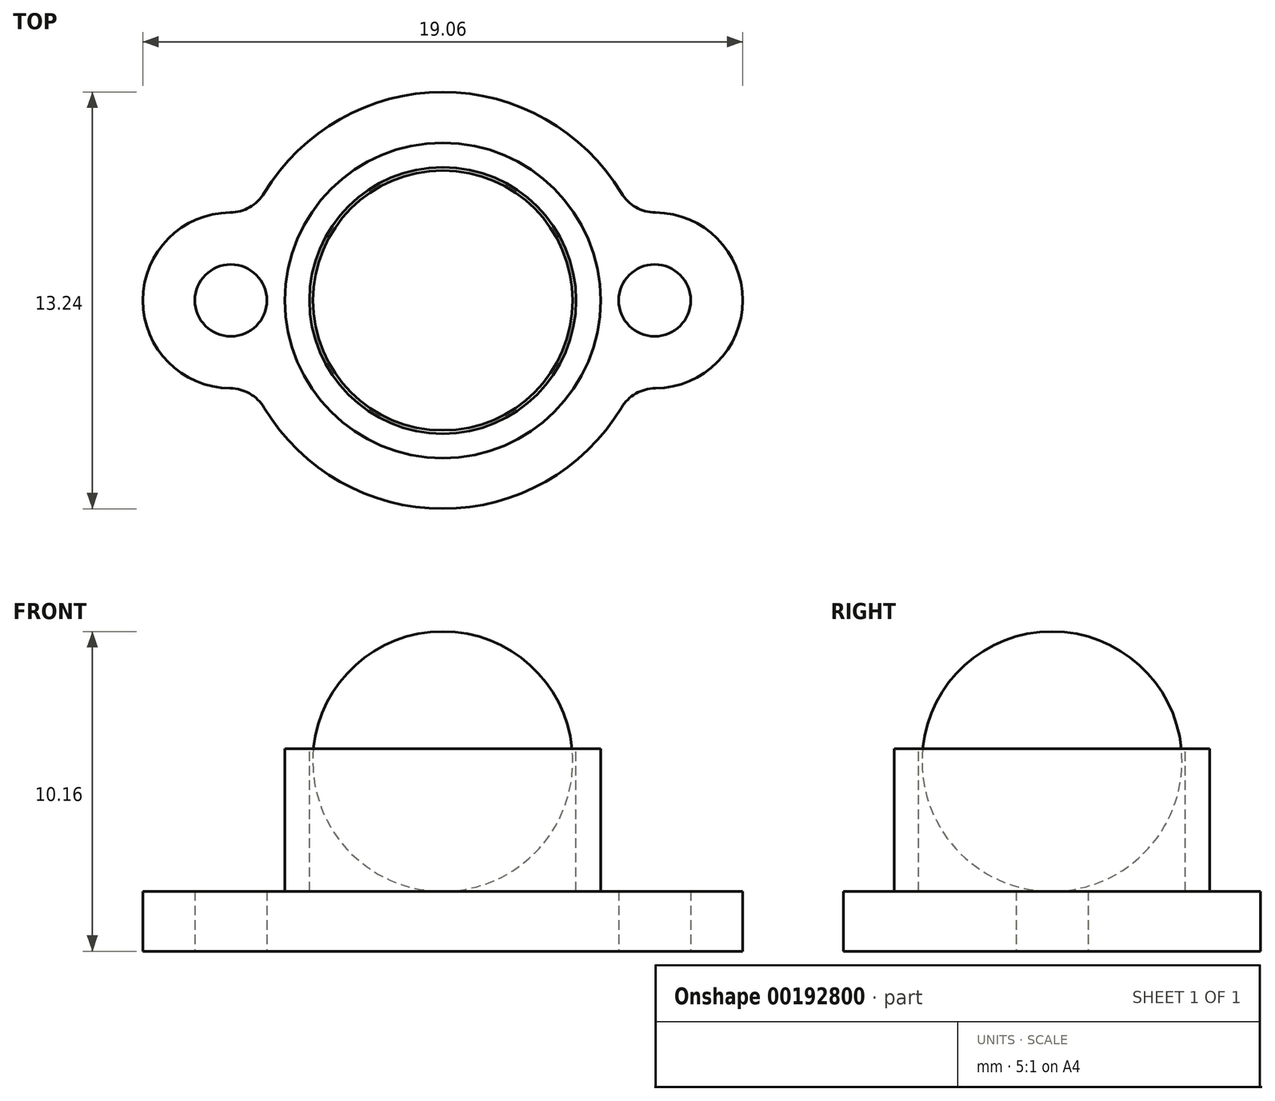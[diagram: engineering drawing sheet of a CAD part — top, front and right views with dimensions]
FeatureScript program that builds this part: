
annotation { "Feature Type Name" : "Feature", "Feature Type Description" : "" }
export const myFeature = defineFeature(function(context is Context, id is Id, definition is map)
    precondition{}
    {
        {
            var Q0;
            Q0=qCreatedBy(makeId("Top.planeOp"),FACE);
            var sketch = newSketch(context, id + "F0", { "sketchPlane" : qUnion([Q0])});
            skArc(sketch, "E0", {"start": v(-5.67, -3.4) * mm, "mid": v(0, -6.62) * mm, "end": v(5.67, -3.4) * mm});
            skCircle(sketch, "E1", {"center": v(-6.73, 0) * mm, "radius": 1.14 * mm});
            skArc(sketch, "E2", {"start": v(-6.75, 2.8) * mm, "mid": v(-9.53, 0) * mm, "end": v(-6.75, -2.8) * mm});
            skPoint(sketch, "E3.visualSharp", {"position": v(-6.04, 2.7) * mm});
            skArc(sketch, "E3.filletArc", {"start": v(-6.75, 2.8) * mm, "mid": v(-6.13, 2.96) * mm, "end": v(-5.67, 3.4) * mm});
            skPoint(sketch, "E4.visualSharp", {"position": v(-6.04, -2.7) * mm});
            skArc(sketch, "E4.filletArc", {"start": v(-5.67, -3.4) * mm, "mid": v(-6.13, -2.96) * mm, "end": v(-6.75, -2.8) * mm});
            skArc(sketch, "E5.MirrorCS", {"start": v(5.67, -3.4) * mm, "mid": v(6.13, -2.96) * mm, "end": v(6.75, -2.8) * mm});
            skArc(sketch, "E6.MirrorCS", {"start": v(6.75, 2.8) * mm, "mid": v(6.13, 2.96) * mm, "end": v(5.67, 3.4) * mm});
            skPoint(sketch, "E7.MirrorP", {"position": v(6.04, -2.7) * mm});
            skCircle(sketch, "E8.MirrorC", {"center": v(6.73, 0) * mm, "radius": 1.14 * mm});
            skArc(sketch, "E9.MirrorCS", {"start": v(6.75, 2.8) * mm, "mid": v(9.53, 0) * mm, "end": v(6.75, -2.8) * mm});
            skPoint(sketch, "E10.MirrorP", {"position": v(6.04, 2.7) * mm});
            skArc(sketch, "E11.trimOffspring", {"start": v(5.67, 3.4) * mm, "mid": v(0, 6.62) * mm, "end": v(-5.67, 3.4) * mm});
            skSolve(sketch);
        }
        {
            var Q0;
            Q0=qSketchRegion(id+"F0",true);
            extrude(context, id + "F1", {"entities" : qUnion([Q0]), "depth" : 1.9 * mm});
        }
        {
            var Q0;
            Q0=qCreatedBy(makeId("Front.planeOp"),FACE);
            var sketch = newSketch(context, id + "F2", { "sketchPlane" : qUnion([Q0])});
            skLineSegment(sketch, "E12", {"start": v(0, 10.16) * mm, "end": v(0, 1.9) * mm});
            skArc(sketch, "E13", {"start": v(0, 1.9) * mm, "mid": v(4.13, 6.03) * mm, "end": v(0, 10.16) * mm});
            skSolve(sketch);
        }
        {
            var Q0;
            Q0=qSketchRegion(id+"F2",true);
            var Q1;
            Q1=sQuery(id+"F2.wireOp",EDGE,"E12");
            revolve(context, id + "F3", {"entities" : qUnion([Q0]), "axis" : qUnion([Q1]), "revolveType" : RevolveType.FULL});
        }
        {
            var Q0;
            Q0=qCreatedBy(makeId("Front.planeOp"),FACE);
            var sketch = newSketch(context, id + "F4", { "sketchPlane" : qUnion([Q0])});
            skLineSegment(sketch, "E14", {"start": v(4.23, 1.9) * mm, "end": v(4.23, 6.43) * mm});
            skLineSegment(sketch, "E15", {"start": v(4.23, 6.43) * mm, "end": v(5.01, 6.43) * mm});
            skLineSegment(sketch, "E16", {"start": v(5.01, 6.43) * mm, "end": v(5.01, 1.9) * mm});
            skLineSegment(sketch, "E17", {"start": v(5.01, 1.9) * mm, "end": v(4.23, 1.9) * mm});
            skLineSegment(sketch, "E18", {"start": v(0, 11.69) * mm, "end": v(0, -1.92) * mm, "construction": true});
            skSolve(sketch);
        }
        {
            var Q0;
            Q0=makeQuery(id+"F4.imprint","IMPRINT",FACE,{"disambiguationData":[TD([[makeQuery(id+"F4.imprint","IMPRINT",EDGE,{"derivedFrom":sQuery(id+"F4.wireOp",EDGE,"E14")}),-1.0]])]});
            var Q1;
            Q1=sQuery(id+"F4.wireOp",EDGE,"E18");
            revolve(context, id + "F5", {"operationType" : NewBodyOperationType.ADD, "entities" : qUnion([Q0]), "axis" : qUnion([Q1]), "revolveType" : RevolveType.FULL});
        }
    });
